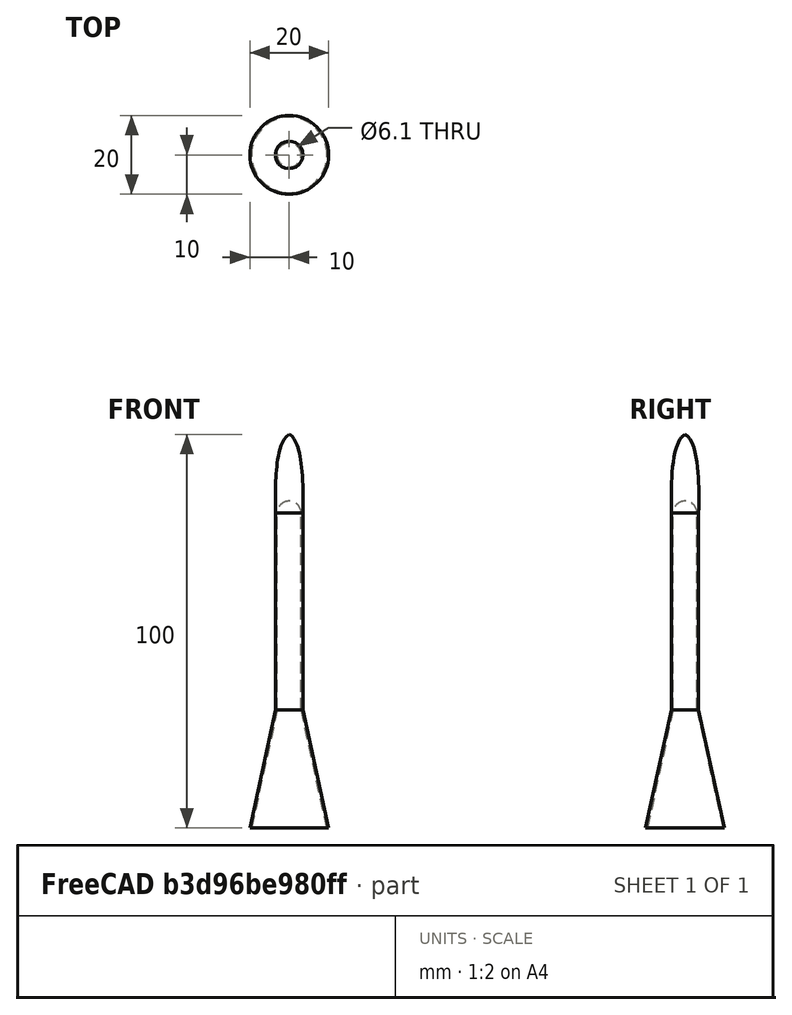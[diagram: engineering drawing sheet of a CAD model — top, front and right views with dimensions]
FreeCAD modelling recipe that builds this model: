
FCSTD DOCUMENT  (FreeCAD 2022.709R28846 (Git))
Label: blow_rocket_v1
License: All rights reserved
LicenseURL: http://en.wikipedia.org/wiki/All_rights_reserved
objects: Spreadsheet::Sheet×1, Sketcher::SketchObject×1, PartDesign::Revolution×1, PartDesign::Body×1
note: 5 computed .brp shape members not serialized (recipe doc carries the construction recipe); baked Part::Feature solids carry a one-line shape summary decoded from their .brp

FEATURE [Spreadsheet::Sheet] Spreadsheet
  PythonMode = false
  ShowCells = 0
  TreeRank = 1
  cells = A2=tube_dia; B2(tube_dia)=5.9; A3=tube tolerance; B3(tube_tol)=0.1; A4=wall thickness; B4(wall_thk)=0.4; A5=body length; B5(l_body)=50; A6=cone length; B6(l_cone)=30; A7=nose length; B7(l_nose)=20; A8=cone bottom diameter; B8(dia_cone_bottom)=20; A9=Nose cone shape coefficients; A10=width coeff; B10(cone_width_coeff)=1.3; A11=heigh coeff; B11(cone_height_coeff)=0.9
FEATURE [Sketcher::SketchObject] Sketch
  ArcFitTolerance = 1e-06
  AttachmentSupport = -> [XZ_Plane]
  FullyConstrained = false
  MapMode = 5
  Placement = pos=(0,0,0) rot=(1,0,0;1.5708rad)
  Support = -> [XZ_Plane]
  TreeRank = 12
  expr: Constraints[16] = Spreadsheet.l_cone
  expr: Constraints[17] = Spreadsheet.l_cone
  expr: Constraints[19] = Spreadsheet.wall_thk
  expr: Constraints[20] = Spreadsheet.l_body
  expr: Constraints[21] = Spreadsheet.l_nose
  expr: Constraints[22] = Spreadsheet.l_nose * Spreadsheet.cone_height_coeff
  expr: Constraints[24] = Spreadsheet.tube_dia / 2 + Spreadsheet.tube_tol
  expr: Constraints[25] = Spreadsheet.dia_cone_bottom / 2
  expr: Constraints[26] = (Spreadsheet.tube_dia / 2 + Spreadsheet.tube_tol) * Spreadsheet.cone_width_coeff
  sketch-geometry (13):
    g0: LineSegment StartX=10 StartY=0 StartZ=0 EndX=9.6 EndY=0 EndZ=0
    g1: LineSegment StartX=9.6 StartY=0 StartZ=0 EndX=3.05 EndY=30 EndZ=0
    g2: LineSegment StartX=3.05 StartY=30 StartZ=0 EndX=3.05 EndY=80 EndZ=0
    g3: LineSegment StartX=10 StartY=0 StartZ=0 EndX=3.45 EndY=30 EndZ=0
    g4: LineSegment StartX=3.45 StartY=30 StartZ=0 EndX=3.45 EndY=80 EndZ=0
    g5: ArcOfCircle CenterX=0 CenterY=80 CenterZ=0 NormalX=0 NormalY=0 NormalZ=1 AngleXU=0 Radius=3.05 StartAngle=-6.5565e-12 EndAngle=1.5708
    g6: Circle [constr] CenterX=3.965 CenterY=98 CenterZ=0 NormalX=0 NormalY=0 NormalZ=1 AngleXU=0 Radius=1
    g7: Circle [constr] CenterX=0 CenterY=100 CenterZ=0 NormalX=0 NormalY=0 NormalZ=1 AngleXU=0 Radius=1
    g8: BSplineCurve PolesCount=3 KnotsCount=2 Degree=2 IsPeriodic=0
    g9: GeomPoint [constr] X=3.45 Y=80 Z=0
    g10: GeomPoint [constr] X=0 Y=100 Z=0
    g11: LineSegment [constr] StartX=3.05 StartY=80 StartZ=0 EndX=3.45 EndY=80 EndZ=0
    g12: LineSegment StartX=0 StartY=83.05 StartZ=0 EndX=0 EndY=100 EndZ=0
  constraints (33):
    c: PointOnObject(g0,g-1)
    c: PointOnObject(g0,g-1)
    c: Coincident(g0,g1)
    c: Coincident(g1,g2)
    c: Vertical(g2)
    c: Coincident(g0,g3)
    c: Coincident(g3,g4)
    c: Vertical(g4)
    c: Coincident(g5,g2)
    c: PointOnObject(g5,g-2)
    c: Coincident(g8,g4)
    c: PointOnObject(g8,g-2)
    c: InternalAlignment(g6,g8)
    c: InternalAlignment(g7,g8)
    c: InternalAlignment(g9,g8)
    c: InternalAlignment(g10,g8)
    c: DistanceY(g-1,g1) = 30
    c: DistanceY(g-1,g3) = 30
    c: Parallel(g1,g3)
    c: DistanceX(g0,g0) = 0.4
    c: DistanceY(g4,g4) = 50
    c: DistanceY(g4,g8) = 20
    c: DistanceY(g4,g6) = 18
    c: Equal(g2,g4)
    c: DistanceX(g-1,g1) = 3.05
    c: DistanceX(g-1,g0) = 10
    c: DistanceX(g-1,g6) = 3.965
    c: PointOnObject(g5,g-2)
    c: Coincident(g11,g4)
    c: Horizontal(g11)
    c: PointOnObject(g5,g11)
    c: Coincident(g12,g8)
    c: Vertical(g12)
FEATURE [PartDesign::Revolution] Revolution
  Angle = 360
  Axis = (0,-2e-16,1)
  Base = (0,0,0)
  ClaimChildren = false
  Fit = 0
  FitJoin = 0
  InnerFit = 0
  InnerFitJoin = 0
  NewSolid = false
  Placement = pos=(0,0,0) rot=(1,0,0;1.5708rad)
  Profile = -> Sketch
  ReferenceAxis = -> Sketch [V_Axis]
  Refine = true
  Reversed = true
  Suppress = false
  TreeRank = 13
  _ProfileBasedVersion = 1
FEATURE [PartDesign::Body] Body
  AutoGroupSolids = false
  ClaimAllChildren = false
  ExportMode = 0
  Group = -> [Sketch,Revolution]
  Origin = -> Origin
  Tip = -> Revolution
  TreeRank = 11
  _ExportChildren = -> [Revolution]
  _GroupVersion = 1
